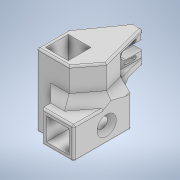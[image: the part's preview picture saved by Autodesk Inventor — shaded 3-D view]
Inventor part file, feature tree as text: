
AUTODESK INVENTOR PART (.ipt)
format: ipt  version: 2022 (Build 260153000, 153)  size: 336,384 bytes
history: native  units: in
note: dims shown in document units (in); Inventor stores cm internally (conversion verified against a paired STEP export)
features: extrude x11, sketch x11, chamfer x4, fillet x1
ambient origin geometry x8: Origin, YZ Plane, XZ Plane, XY Plane, X Axis, Y Axis, Z Axis, Center Point
bodies: Solid1 (feature_tree)
feature tree (27):
  extrude  "Extrusion1"  Depth=1.4173in
  extrude  "Extrusion2"  Depth=2.5906in
  extrude  "Extrusion3"  Depth=1.0236in TaperAngle=0.0deg
  extrude  "Extrusion4"  Depth=1.0236in
  extrude  "Extrusion5"  Depth=1.0236in
  chamfer  "Chamfer3"  Distance=2.3937in
  chamfer  "Chamfer4"  Distance=2.7559in
  extrude  "Extrusion6"  Depth=0.1969in TaperAngle=45.0deg
  extrude  "Extrusion7"  Depth=1.4567in
  extrude  "Extrusion8"  Depth=0.1969in
  extrude  "Extrusion10"  Depth=0.1575in
  extrude  "Extrusion11"  Depth=0.1575in
  extrude  "Extrusion12"  Depth=0.1575in
  chamfer  "Chamfer5"  Distance=0.1575in
  chamfer  "Chamfer6"  Distance=0.4331in
  fillet  "Fillet2"  Radius=1.3268in
  sketch  "Sketch1"  dims[d0=1.4173in d1=1.4173in]
  sketch  "Sketch2"  dims[d2=2.5906in d3=0.0in d4=2.5906in]
  sketch  "Sketch3"  dims[d5=1.4173in d6=1.0236in d7=0.3937in d8=0.0in d9=0.0in]
  sketch  "Sketch4"  dims[d10=1.0236in d11=1.0236in]
  sketch  "Sketch5"  dims[d12=2.3937in d13=0.0in d14=1.0236in]
  sketch  "Sketch6"  dims[d15=1.0236in d16=2.3937in d17=0.0in]
  sketch  "Sketch7"  dims[d24=0.4724in d25=2.7559in d26=0.0in]
  sketch  "Sketch8"  dims[d27=0.1969in d28=0.0787in d29=45.0deg d30=0.1969in d31=0.0787in d32=45.0deg]
  sketch  "Sketch10"  dims[d34=1.2205in d35=1.4567in]
  sketch  "Sketch11"  dims[d36=1.3268in d37=1.811in d38=0.0in d39=0.0in d40=0.1969in]
  sketch  "Sketch12"  dims[d41=0.4331in d42=0.1575in d43=0.1575in d44=0.1575in d45=0.1575in d46=0.4331in d47=1.3268in d48=0.0in d49=0.6772in d50=0.0in d54=0.8268in d55=0.9843in d56=1.2795in d57=0.0in d58=0.1575in d59=0.315in d60=1.2205in d61=0.0in d62=1.4567in d63=0.0in d64=0.9843in d65=0.0787in d66=45.0deg d67=0.3937in d68=0.0787in d69=45.0deg d70=0.0787in]
